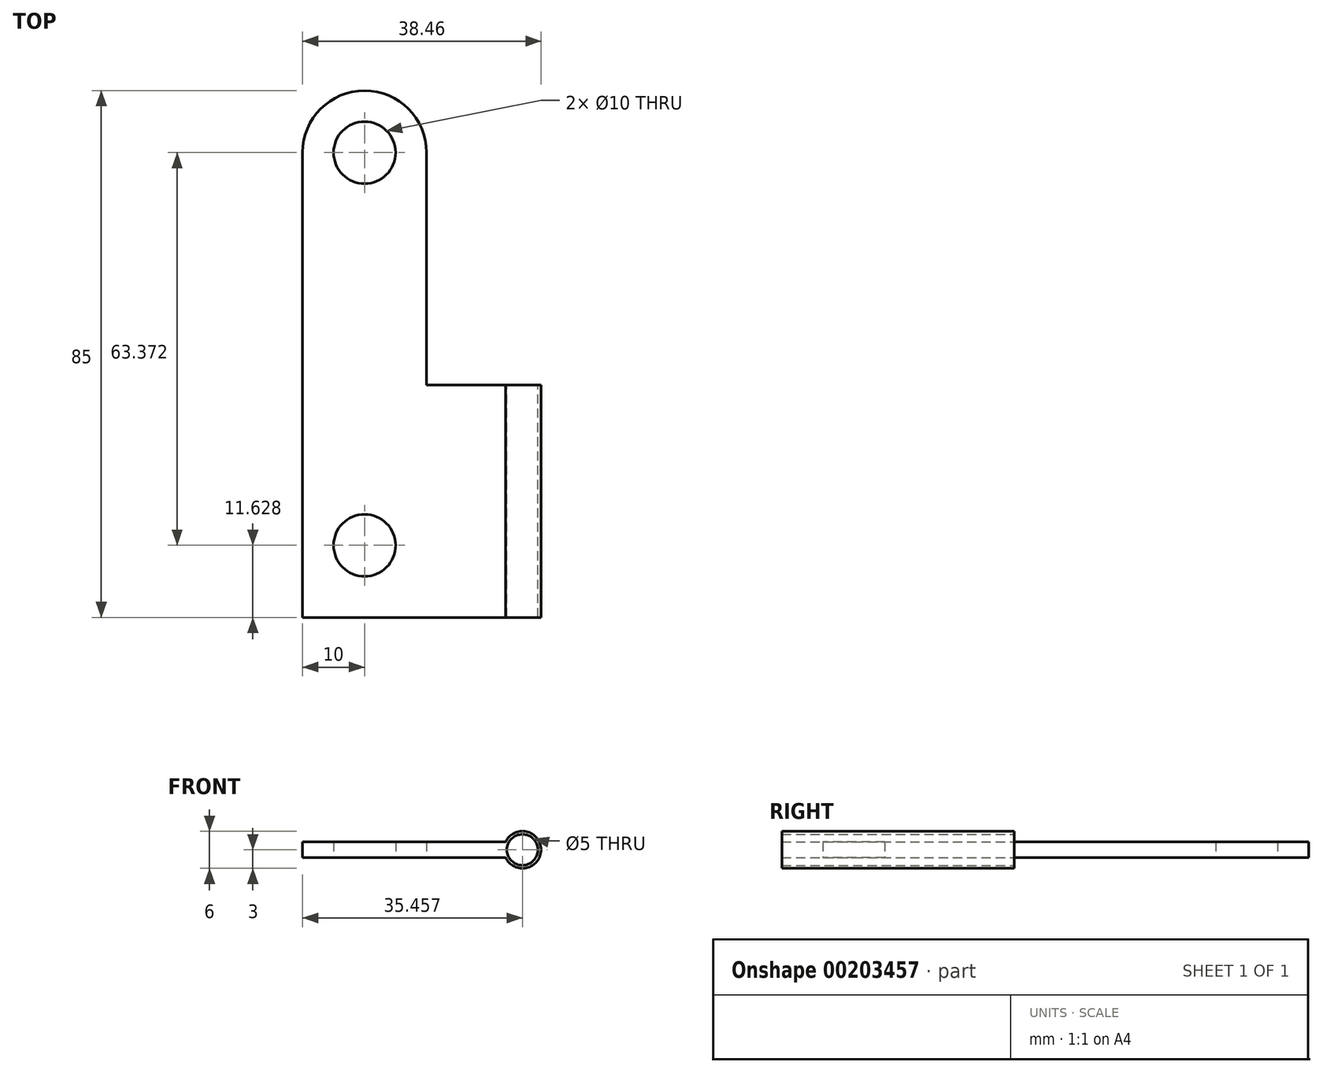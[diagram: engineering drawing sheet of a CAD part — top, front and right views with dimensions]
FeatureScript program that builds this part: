
annotation { "Feature Type Name" : "Feature", "Feature Type Description" : "" }
export const myFeature = defineFeature(function(context is Context, id is Id, definition is map)
    precondition{}
    {
        {
            var Q0;
            Q0=qCreatedBy(makeId("Top.planeOp"),FACE);
            var sketch = newSketch(context, id + "F0", { "sketchPlane" : qUnion([Q0])});
            skLineSegment(sketch, "E0.bottom", {"start": v(0, 0) * mm, "end": v(20, 0) * mm});
            skLineSegment(sketch, "E0.top", {"start": v(0, 75) * mm, "end": v(20, 75) * mm});
            skLineSegment(sketch, "E0.left", {"start": v(0, 0) * mm, "end": v(0, 75) * mm});
            skLineSegment(sketch, "E0.right", {"start": v(20, 0) * mm, "end": v(20, 75) * mm});
            skCircle(sketch, "E1", {"center": v(10, 75) * mm, "radius": 10 * mm});
            skLineSegment(sketch, "E2.bottom", {"start": v(20, 0) * mm, "end": v(35.46, 0) * mm});
            skLineSegment(sketch, "E2.top", {"start": v(20, 37.5) * mm, "end": v(35.46, 37.5) * mm});
            skLineSegment(sketch, "E2.left", {"start": v(20, 0) * mm, "end": v(20, 37.5) * mm});
            skLineSegment(sketch, "E2.right", {"start": v(35.46, 0) * mm, "end": v(35.46, 37.5) * mm});
            skCircle(sketch, "E3", {"center": v(10, 75) * mm, "radius": 5 * mm});
            skCircle(sketch, "E4", {"center": v(10, 11.63) * mm, "radius": 5 * mm});
            skSolve(sketch);
        }
        {
            var Q0;
            Q0 = qSketchRegion(id + "F0", true);
            extrude(context, id + "F1", {"entities" : qUnion([Q0]), "depth" : 2.5 * mm});
        }
        {
            var Q0;
            Q0=makeQuery(id+"F1.opExtrude","SWEPT_FACE",FACE,{"disambiguationData":[OSD([sQuery(id+"F0.wireOp",EDGE,"E2.top")])]});
            var sketch = newSketch(context, id + "F2", { "sketchPlane" : qUnion([Q0])});
            skCircle(sketch, "E5", {"center": v(-35.46, 1.25) * mm, "radius": 3 * mm});
            skCircle(sketch, "E6", {"center": v(-35.46, 1.25) * mm, "radius": 2.5 * mm});
            skSolve(sketch);
        }
        {
            var Q0;
            {var subQ1=sQuery(id+"F0.wireOp",EDGE,"E2.top");var subQ6=makeQuery(id+"F1.opExtrude","SWEPT_EDGE",EDGE,{"disambiguationData":[OSD([subQ1,sQuery(id+"F0.wireOp",EDGE,"E2.right")])]});Q0=makeQuery(id+"F2.imprint","IMPRINT",FACE,{"disambiguationData":[TD([[makeQuery(id+"F2.imprint","IMPRINT",EDGE,{"derivedFrom":subQ6}),1.0]])]});}
            extrude(context, id + "F3", {"entities" : qUnion([Q0]), "operationType" : NewBodyOperationType.REMOVE, "endBound" : BoundingType.THROUGH_ALL, "oppositeDirection" : true, "depth" : 37.5 * mm});
        }
        {
            var Q0;
            Q0 = qSketchRegion(id + "F2", true);
            extrude(context, id + "F4", {"entities" : qUnion([Q0]), "operationType" : NewBodyOperationType.ADD, "oppositeDirection" : true, "depth" : 37.5 * mm});
        }
    });
